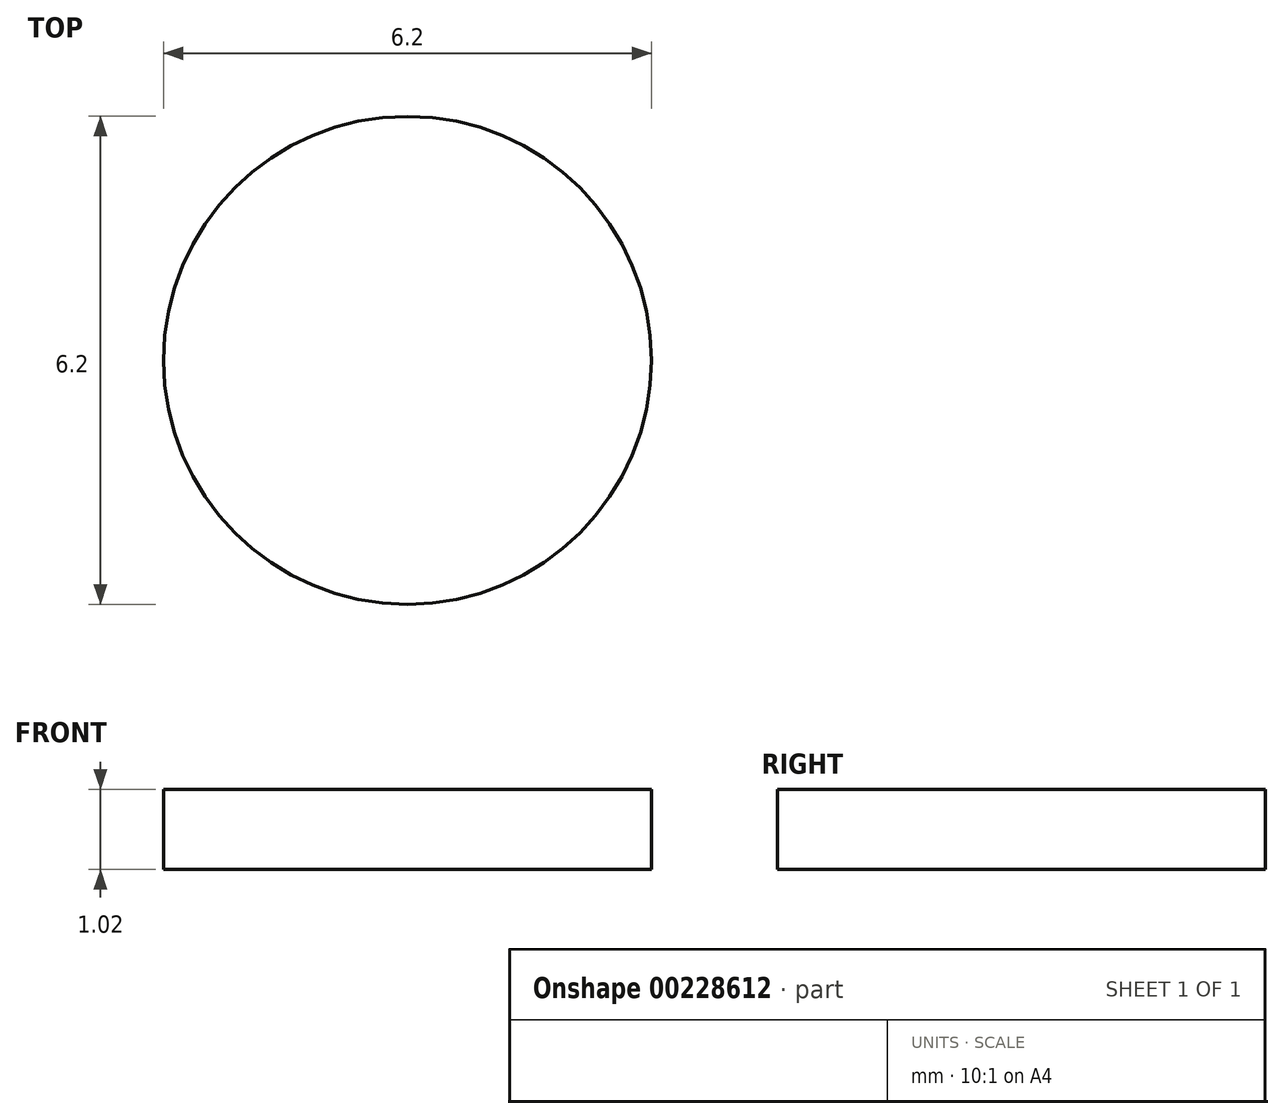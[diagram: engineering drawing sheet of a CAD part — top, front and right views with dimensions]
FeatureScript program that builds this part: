
annotation { "Feature Type Name" : "Feature", "Feature Type Description" : "" }
export const myFeature = defineFeature(function(context is Context, id is Id, definition is map)
    precondition{}
    {
        {
            var Q0;
            Q0=qCreatedBy(makeId("Top.planeOp"),FACE);
            var sketch = newSketch(context, id + "F0", { "sketchPlane" : qUnion([Q0])});
            skCircle(sketch, "E0", {"center": v(0, 0) * mm, "radius": 3.1 * mm});
            skSolve(sketch);
        }
        {
            var Q0;
            Q0 = qSketchRegion(id + "F0", true);
            extrude(context, id + "F1", {"entities" : qUnion([Q0]), "depth" : 1.02 * mm});
        }
    });
